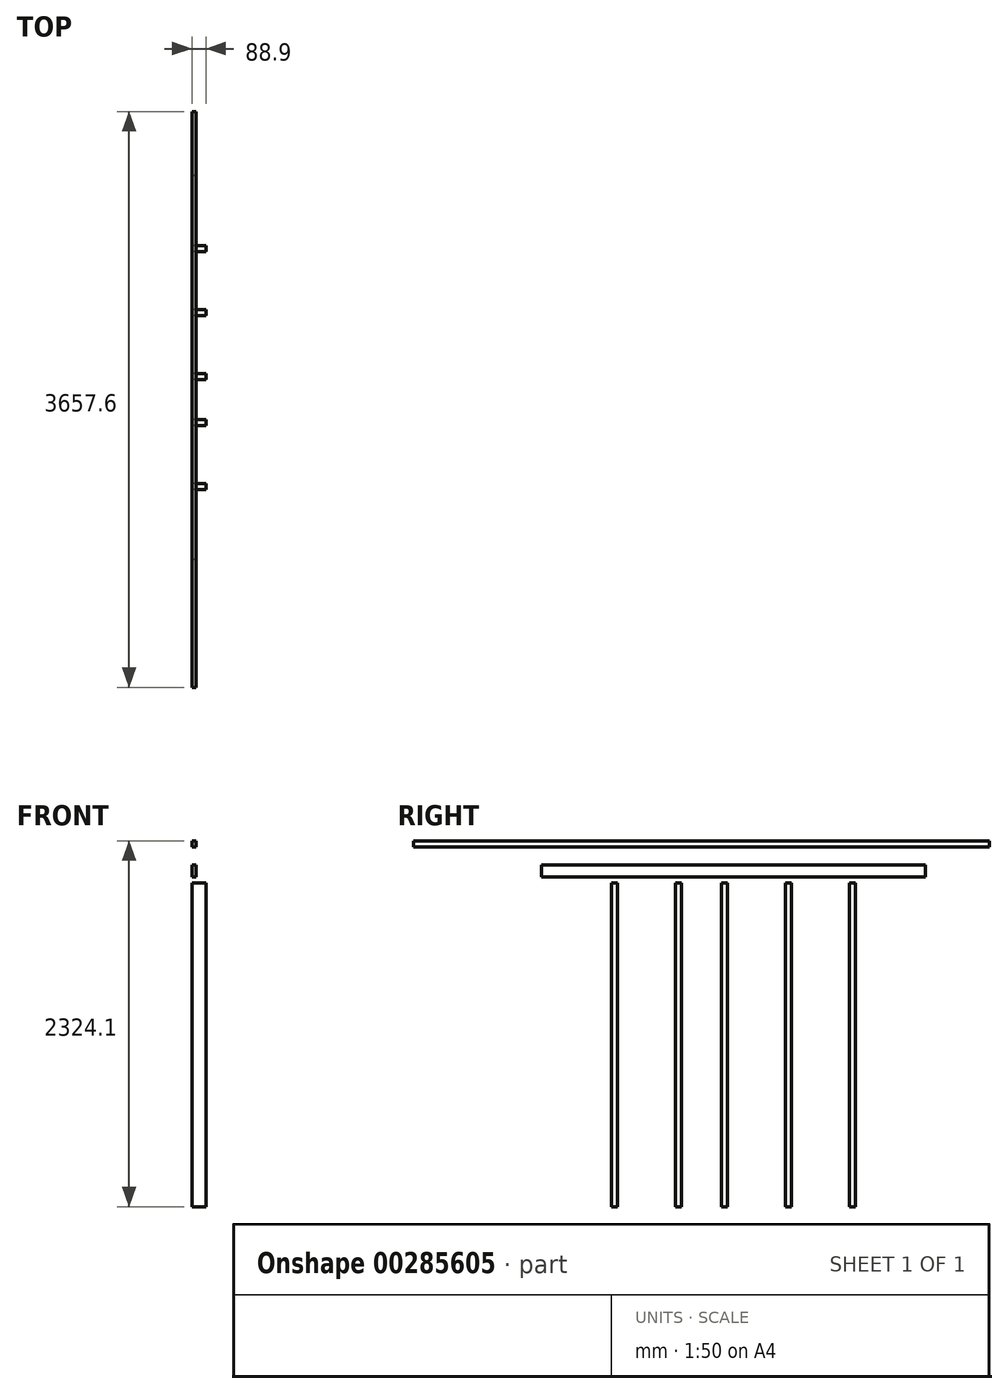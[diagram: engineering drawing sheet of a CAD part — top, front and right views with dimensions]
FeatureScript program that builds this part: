
annotation { "Feature Type Name" : "Feature", "Feature Type Description" : "" }
export const myFeature = defineFeature(function(context is Context, id is Id, definition is map)
    precondition{}
    {
        {
            var Q0;
            Q0=qCreatedBy(makeId("Right.planeOp"),FACE);
            var sketch = newSketch(context, id + "F0", { "sketchPlane" : qUnion([Q0])});
            skLineSegment(sketch, "E0.bottom", {"start": v(-1828.8, -1219.2) * mm, "end": v(1828.8, -1219.2) * mm});
            skLineSegment(sketch, "E0.top", {"start": v(-1828.8, 1219.2) * mm, "end": v(1828.8, 1219.2) * mm});
            skLineSegment(sketch, "E0.left", {"start": v(-1828.8, -1219.2) * mm, "end": v(-1828.8, 1219.2) * mm});
            skLineSegment(sketch, "E0.right", {"start": v(1828.8, -1219.2) * mm, "end": v(1828.8, 1219.2) * mm});
            skPoint(sketch, "E0.middle", {"position": v(0, 0) * mm});
            skLineSegment(sketch, "E1.bottom", {"start": v(-1828.8, -1219.2) * mm, "end": v(0, -1219.2) * mm});
            skLineSegment(sketch, "E1.top", {"start": v(-1828.8, -1181.1) * mm, "end": v(0, -1181.1) * mm});
            skLineSegment(sketch, "E1.left", {"start": v(-1828.8, -1219.2) * mm, "end": v(-1828.8, -1181.1) * mm});
            skLineSegment(sketch, "E2.top", {"start": v(-1828.8, 1181.1) * mm, "end": v(1828.8, 1181.1) * mm});
            skLineSegment(sketch, "E2.left", {"start": v(-1828.8, 1219.2) * mm, "end": v(-1828.8, 1181.1) * mm});
            skLineSegment(sketch, "E2.right", {"start": v(1828.8, 1219.2) * mm, "end": v(1828.8, 1181.1) * mm});
            skLineSegment(sketch, "E3.bottom", {"start": v(-1828.8, 1181.1) * mm, "end": v(0, 1181.1) * mm});
            skLineSegment(sketch, "E3.top", {"start": v(-1828.8, 1143) * mm, "end": v(0, 1143) * mm});
            skLineSegment(sketch, "E3.left", {"start": v(-1828.8, 1181.1) * mm, "end": v(-1828.8, 1143) * mm});
            skLineSegment(sketch, "E4.bottom", {"start": v(0, 1143) * mm, "end": v(1828.8, 1143) * mm});
            skLineSegment(sketch, "E4.top", {"start": v(0, 1181.1) * mm, "end": v(1828.8, 1181.1) * mm});
            skLineSegment(sketch, "E4.right", {"start": v(1828.8, 1143) * mm, "end": v(1828.8, 1181.1) * mm});
            skLineSegment(sketch, "E5.bottom", {"start": v(0, -1219.2) * mm, "end": v(1828.8, -1219.2) * mm});
            skLineSegment(sketch, "E5.top", {"start": v(0, -1181.1) * mm, "end": v(1828.8, -1181.1) * mm});
            skLineSegment(sketch, "E5.right", {"start": v(1828.8, -1219.2) * mm, "end": v(1828.8, -1181.1) * mm});
            skLineSegment(sketch, "E6.bottom", {"start": v(-1828.8, -1181.1) * mm, "end": v(1828.8, -1181.1) * mm});
            skLineSegment(sketch, "E6.top", {"start": v(-1828.8, -1143) * mm, "end": v(1828.8, -1143) * mm});
            skLineSegment(sketch, "E6.left", {"start": v(-1828.8, -1181.1) * mm, "end": v(-1828.8, -1143) * mm});
            skLineSegment(sketch, "E6.right", {"start": v(1828.8, -1181.1) * mm, "end": v(1828.8, -1143) * mm});
            skLineSegment(sketch, "E7.bottom", {"start": v(0, 1143) * mm, "end": v(38.1, 1143) * mm});
            skLineSegment(sketch, "E7.top", {"start": v(0, -1143) * mm, "end": v(38.1, -1143) * mm});
            skLineSegment(sketch, "E8.bottom", {"start": v(0, 1143) * mm, "end": v(-38.1, 1143) * mm});
            skLineSegment(sketch, "E8.top", {"start": v(0, -1143) * mm, "end": v(-38.1, -1143) * mm});
            skLineSegment(sketch, "E9.bottom", {"start": v(1828.8, 1143) * mm, "end": v(1792.72, 1143) * mm});
            skLineSegment(sketch, "E9.top", {"start": v(1828.8, -1143) * mm, "end": v(1792.72, -1143) * mm});
            skLineSegment(sketch, "E9.left", {"start": v(1828.8, 1143) * mm, "end": v(1828.8, -1143) * mm});
            skLineSegment(sketch, "E9.right", {"start": v(1792.72, 1143) * mm, "end": v(1792.72, -1143) * mm});
            skLineSegment(sketch, "E10.bottom", {"start": v(-1828.8, -1143) * mm, "end": v(-1790.7, -1143) * mm});
            skLineSegment(sketch, "E10.top", {"start": v(-1828.8, 1143) * mm, "end": v(-1790.7, 1143) * mm});
            skLineSegment(sketch, "E10.left", {"start": v(-1828.8, -1143) * mm, "end": v(-1828.8, 1143) * mm});
            skLineSegment(sketch, "E10.right", {"start": v(-1790.7, -1143) * mm, "end": v(-1790.7, 1143) * mm});
            skPoint(sketch, "E11.orphan", {"position": v(0, 1219.2) * mm});
            skLineSegment(sketch, "E12", {"start": v(-1828.8, -1143) * mm, "end": v(-1384.3, -1143) * mm});
            skLineSegment(sketch, "E13", {"start": v(-1384.3, -1143) * mm, "end": v(-977.9, -1143) * mm});
            skLineSegment(sketch, "E14", {"start": v(-977.9, -1143) * mm, "end": v(-571.5, -1143) * mm});
            skLineSegment(sketch, "E15", {"start": v(-571.5, -1143) * mm, "end": v(-165.1, -1143) * mm});
            skLineSegment(sketch, "E16.bottom", {"start": v(-1384.3, -1143) * mm, "end": v(-1384.3, -1143) * mm});
            skLineSegment(sketch, "E16.top", {"start": v(-1384.3, 1143) * mm, "end": v(-1384.3, 1143) * mm});
            skLineSegment(sketch, "E16.left", {"start": v(-1384.3, -1143) * mm, "end": v(-1384.3, 1143) * mm});
            skLineSegment(sketch, "E16.right", {"start": v(-1384.3, -1143) * mm, "end": v(-1384.3, 1143) * mm});
            skLineSegment(sketch, "E17.bottom", {"start": v(-977.9, -1143) * mm, "end": v(-977.9, -1143) * mm});
            skLineSegment(sketch, "E17.top", {"start": v(-977.9, 1143) * mm, "end": v(-977.9, 1143) * mm});
            skLineSegment(sketch, "E17.left", {"start": v(-977.9, -1143) * mm, "end": v(-977.9, 990.6) * mm});
            skLineSegment(sketch, "E17.right", {"start": v(-977.9, -1143) * mm, "end": v(-977.9, 990.6) * mm});
            skLineSegment(sketch, "E18.bottom", {"start": v(-571.5, -1143) * mm, "end": v(-571.5, -1143) * mm});
            skLineSegment(sketch, "E18.top", {"start": v(-571.5, 1143) * mm, "end": v(-571.5, 1143) * mm});
            skLineSegment(sketch, "E18.right", {"start": v(-571.5, -1104.9) * mm, "end": v(-571.5, 952.5) * mm});
            skLineSegment(sketch, "E19.bottom", {"start": v(-165.1, -1143) * mm, "end": v(-165.1, -1143) * mm});
            skLineSegment(sketch, "E19.top", {"start": v(-165.1, 1143) * mm, "end": v(-165.1, 1143) * mm});
            skLineSegment(sketch, "E19.left", {"start": v(-165.1, -1104.9) * mm, "end": v(-165.1, 952.5) * mm});
            skLineSegment(sketch, "E19.right", {"start": v(-165.1, -1104.9) * mm, "end": v(-165.1, 952.5) * mm});
            skLineSegment(sketch, "E20", {"start": v(1828.8, -1143) * mm, "end": v(1384.3, -1143) * mm});
            skLineSegment(sketch, "E21", {"start": v(1384.3, -1143) * mm, "end": v(977.9, -1143) * mm});
            skLineSegment(sketch, "E22", {"start": v(977.9, -1143) * mm, "end": v(571.5, -1143) * mm});
            skLineSegment(sketch, "E23", {"start": v(571.5, -1143) * mm, "end": v(165.1, -1143) * mm});
            skLineSegment(sketch, "E24.bottom", {"start": v(1384.3, -1143) * mm, "end": v(1384.3, -1143) * mm});
            skLineSegment(sketch, "E24.top", {"start": v(1384.3, 1143) * mm, "end": v(1384.3, 1143) * mm});
            skLineSegment(sketch, "E24.left", {"start": v(1384.3, -1143) * mm, "end": v(1384.3, 990.6) * mm});
            skLineSegment(sketch, "E24.right", {"start": v(1384.3, -1143) * mm, "end": v(1384.3, 990.6) * mm});
            skLineSegment(sketch, "E25.bottom", {"start": v(977.9, -1143) * mm, "end": v(977.9, -1143) * mm});
            skLineSegment(sketch, "E25.top", {"start": v(977.9, 1143) * mm, "end": v(977.9, 1143) * mm});
            skLineSegment(sketch, "E25.left", {"start": v(977.9, -1104.9) * mm, "end": v(977.9, 952.5) * mm});
            skLineSegment(sketch, "E26.bottom", {"start": v(571.5, -1143) * mm, "end": v(571.5, -1143) * mm});
            skLineSegment(sketch, "E26.top", {"start": v(571.5, 1143) * mm, "end": v(571.5, 1143) * mm});
            skLineSegment(sketch, "E26.left", {"start": v(571.5, -1104.9) * mm, "end": v(571.5, 952.5) * mm});
            skLineSegment(sketch, "E26.right", {"start": v(571.5, -1104.9) * mm, "end": v(571.5, 952.5) * mm});
            skLineSegment(sketch, "E27.bottom", {"start": v(165.1, -1143) * mm, "end": v(165.1, -1143) * mm});
            skLineSegment(sketch, "E27.top", {"start": v(165.1, 1143) * mm, "end": v(165.1, 1143) * mm});
            skLineSegment(sketch, "E27.left", {"start": v(165.1, -1104.9) * mm, "end": v(165.1, 952.5) * mm});
            skLineSegment(sketch, "E27.right", {"start": v(165.1, -1104.9) * mm, "end": v(165.1, 952.5) * mm});
            skLineSegment(sketch, "E28.bottom", {"start": v(1384.3, -1143) * mm, "end": v(1346.2, -1143) * mm});
            skLineSegment(sketch, "E28.top", {"start": v(1384.3, 1143) * mm, "end": v(1346.2, 1143) * mm});
            skLineSegment(sketch, "E28.right", {"start": v(1346.2, -1143) * mm, "end": v(1346.2, 990.6) * mm});
            skLineSegment(sketch, "E29.bottom", {"start": v(977.9, -1143) * mm, "end": v(939.8, -1143) * mm});
            skLineSegment(sketch, "E29.top", {"start": v(977.9, 1143) * mm, "end": v(939.8, 1143) * mm});
            skLineSegment(sketch, "E29.right", {"start": v(939.8, -1104.9) * mm, "end": v(939.8, 952.5) * mm});
            skLineSegment(sketch, "E30.bottom", {"start": v(571.5, -1143) * mm, "end": v(533.4, -1143) * mm});
            skLineSegment(sketch, "E30.top", {"start": v(571.5, 1143) * mm, "end": v(533.4, 1143) * mm});
            skLineSegment(sketch, "E30.right", {"start": v(533.4, -1104.9) * mm, "end": v(533.4, 952.5) * mm});
            skLineSegment(sketch, "E31.bottom", {"start": v(-1384.3, -1143) * mm, "end": v(-1346.2, -1143) * mm});
            skLineSegment(sketch, "E31.top", {"start": v(-1384.3, 1143) * mm, "end": v(-1346.2, 1143) * mm});
            skLineSegment(sketch, "E31.right", {"start": v(-1346.2, -1143) * mm, "end": v(-1346.2, 1143) * mm});
            skLineSegment(sketch, "E32.bottom", {"start": v(-977.9, -1143) * mm, "end": v(-939.8, -1143) * mm});
            skLineSegment(sketch, "E32.top", {"start": v(-977.9, 1143) * mm, "end": v(-939.8, 1143) * mm});
            skLineSegment(sketch, "E32.right", {"start": v(-939.8, -1143) * mm, "end": v(-939.8, 990.6) * mm});
            skLineSegment(sketch, "E33.bottom", {"start": v(-571.5, -1143) * mm, "end": v(-533.4, -1143) * mm});
            skLineSegment(sketch, "E33.top", {"start": v(-571.5, 1143) * mm, "end": v(-533.4, 1143) * mm});
            skLineSegment(sketch, "E33.right", {"start": v(-533.4, -1104.9) * mm, "end": v(-533.4, 952.5) * mm});
            skLineSegment(sketch, "E34.bottom", {"start": v(-165.1, -1143) * mm, "end": v(-127, -1143) * mm});
            skLineSegment(sketch, "E34.top", {"start": v(-165.1, 1143) * mm, "end": v(-127, 1143) * mm});
            skLineSegment(sketch, "E34.right", {"start": v(-127, -1104.9) * mm, "end": v(-127, 952.5) * mm});
            skLineSegment(sketch, "E35.bottom", {"start": v(165.1, -1143) * mm, "end": v(127, -1143) * mm});
            skLineSegment(sketch, "E35.top", {"start": v(165.1, 1143) * mm, "end": v(127, 1143) * mm});
            skLineSegment(sketch, "E35.right", {"start": v(127, -1104.9) * mm, "end": v(127, 952.5) * mm});
            skLineSegment(sketch, "E36.bottom", {"start": v(1792.72, -1143) * mm, "end": v(1754.62, -1143) * mm});
            skLineSegment(sketch, "E36.top", {"start": v(1792.72, 1143) * mm, "end": v(1754.62, 1143) * mm});
            skLineSegment(sketch, "E36.left", {"start": v(1792.72, -1143) * mm, "end": v(1792.72, 1143) * mm});
            skLineSegment(sketch, "E36.right", {"start": v(1754.62, -1143) * mm, "end": v(1754.62, 1143) * mm});
            skLineSegment(sketch, "E37.bottom", {"start": v(-1790.7, -1143) * mm, "end": v(-1752.6, -1143) * mm});
            skLineSegment(sketch, "E37.top", {"start": v(-1790.7, 1143) * mm, "end": v(-1752.6, 1143) * mm});
            skLineSegment(sketch, "E37.right", {"start": v(-1752.6, -1143) * mm, "end": v(-1752.6, 1143) * mm});
            skLineSegment(sketch, "E38", {"start": v(0, -1143) * mm, "end": v(0, 990.6) * mm});
            skLineSegment(sketch, "E39", {"start": v(0, 990.6) * mm, "end": v(1346.2, 990.6) * mm});
            skLineSegment(sketch, "E40", {"start": v(1346.2, 990.6) * mm, "end": v(1346.2, -1143) * mm});
            skLineSegment(sketch, "E41", {"start": v(0, 990.6) * mm, "end": v(-939.8, 990.6) * mm});
            skLineSegment(sketch, "E42", {"start": v(-939.8, 990.6) * mm, "end": v(-939.8, -1143) * mm});
            skLineSegment(sketch, "E43.top", {"start": v(0, 952.5) * mm, "end": v(1346.2, 952.5) * mm});
            skLineSegment(sketch, "E43.left", {"start": v(0, 990.6) * mm, "end": v(0, 952.5) * mm});
            skLineSegment(sketch, "E43.right", {"start": v(1346.2, 990.6) * mm, "end": v(1346.2, 952.5) * mm});
            skLineSegment(sketch, "E44.top", {"start": v(0, 952.5) * mm, "end": v(-939.8, 952.5) * mm});
            skLineSegment(sketch, "E44.right", {"start": v(-939.8, 990.6) * mm, "end": v(-939.8, 952.5) * mm});
            skLineSegment(sketch, "E45.bottom", {"start": v(-939.8, -1143) * mm, "end": v(0, -1143) * mm});
            skLineSegment(sketch, "E45.top", {"start": v(-939.8, -1104.9) * mm, "end": v(0, -1104.9) * mm});
            skLineSegment(sketch, "E45.left", {"start": v(-939.8, -1143) * mm, "end": v(-939.8, -1104.9) * mm});
            skLineSegment(sketch, "E45.right", {"start": v(0, -1143) * mm, "end": v(0, -1104.9) * mm});
            skLineSegment(sketch, "E46.bottom", {"start": v(0, -1143) * mm, "end": v(1346.2, -1143) * mm});
            skLineSegment(sketch, "E46.top", {"start": v(0, -1104.9) * mm, "end": v(1346.2, -1104.9) * mm});
            skLineSegment(sketch, "E46.right", {"start": v(1346.2, -1143) * mm, "end": v(1346.2, -1104.9) * mm});
            skLineSegment(sketch, "E47.bottom", {"start": v(0, 952.5) * mm, "end": v(-38.1, 952.5) * mm});
            skLineSegment(sketch, "E47.top", {"start": v(0, -1104.9) * mm, "end": v(-38.1, -1104.9) * mm});
            skLineSegment(sketch, "E47.left", {"start": v(0, 952.5) * mm, "end": v(0, -1104.9) * mm});
            skLineSegment(sketch, "E47.right", {"start": v(-38.1, 952.5) * mm, "end": v(-38.1, -1104.9) * mm});
            skLineSegment(sketch, "E48.bottom", {"start": v(0, 952.5) * mm, "end": v(38.1, 952.5) * mm});
            skLineSegment(sketch, "E48.top", {"start": v(0, -1104.9) * mm, "end": v(38.1, -1104.9) * mm});
            skLineSegment(sketch, "E48.right", {"start": v(38.1, 952.5) * mm, "end": v(38.1, -1104.9) * mm});
            skLineSegment(sketch, "E49.bottom", {"start": v(-939.8, 952.5) * mm, "end": v(-901.7, 952.5) * mm});
            skLineSegment(sketch, "E49.top", {"start": v(-939.8, -1104.9) * mm, "end": v(-901.7, -1104.9) * mm});
            skLineSegment(sketch, "E49.left", {"start": v(-939.8, 952.5) * mm, "end": v(-939.8, -1104.9) * mm});
            skLineSegment(sketch, "E49.right", {"start": v(-901.7, 952.5) * mm, "end": v(-901.7, -1104.9) * mm});
            skLineSegment(sketch, "E50.bottom", {"start": v(1346.2, 952.5) * mm, "end": v(1308.1, 952.5) * mm});
            skLineSegment(sketch, "E50.top", {"start": v(1346.2, -1104.9) * mm, "end": v(1308.1, -1104.9) * mm});
            skLineSegment(sketch, "E50.left", {"start": v(1346.2, 952.5) * mm, "end": v(1346.2, -1104.9) * mm});
            skLineSegment(sketch, "E50.right", {"start": v(1308.1, 952.5) * mm, "end": v(1308.1, -1104.9) * mm});
            skLineSegment(sketch, "E51.bottom", {"start": v(1346.2, 990.6) * mm, "end": v(-939.8, 990.6) * mm});
            skLineSegment(sketch, "E51.top", {"start": v(1346.2, 1066.8) * mm, "end": v(-939.8, 1066.8) * mm});
            skLineSegment(sketch, "E52.top", {"start": v(1346.2, 1028.7) * mm, "end": v(-939.8, 1028.7) * mm});
            skLineSegment(sketch, "E53", {"start": v(977.9, 1066.8) * mm, "end": v(977.9, 1143) * mm});
            skLineSegment(sketch, "E54", {"start": v(939.8, 1066.8) * mm, "end": v(939.8, 1143) * mm});
            skLineSegment(sketch, "E55", {"start": v(571.5, 1066.8) * mm, "end": v(571.5, 1143) * mm});
            skLineSegment(sketch, "E56", {"start": v(533.4, 1066.8) * mm, "end": v(533.4, 1143) * mm});
            skLineSegment(sketch, "E57", {"start": v(165.1, 1066.8) * mm, "end": v(165.1, 1143) * mm});
            skLineSegment(sketch, "E58", {"start": v(127, 1066.8) * mm, "end": v(127, 1143) * mm});
            skLineSegment(sketch, "E59", {"start": v(-127, 1066.8) * mm, "end": v(-127, 1143) * mm});
            skLineSegment(sketch, "E60", {"start": v(-165.1, 1066.8) * mm, "end": v(-165.1, 1143) * mm});
            skLineSegment(sketch, "E61", {"start": v(-533.4, 1066.8) * mm, "end": v(-533.4, 1143) * mm});
            skPoint(sketch, "E62.trimOffspring.start.orphan", {"position": v(977.9, 990.6) * mm});
            skLineSegment(sketch, "E63.trimOffspring", {"start": v(-571.5, 1066.8) * mm, "end": v(-571.5, 1143) * mm});
            skLineSegment(sketch, "E64.bottom", {"start": v(-977.9, 1143) * mm, "end": v(-1016, 1143) * mm});
            skLineSegment(sketch, "E64.top", {"start": v(-977.9, -1143) * mm, "end": v(-1016, -1143) * mm});
            skLineSegment(sketch, "E64.left", {"start": v(-977.9, 1143) * mm, "end": v(-977.9, 1066.8) * mm});
            skLineSegment(sketch, "E64.right", {"start": v(-1016, 1143) * mm, "end": v(-1016, -1143) * mm});
            skLineSegment(sketch, "E65.bottom", {"start": v(1384.3, 1143) * mm, "end": v(1422.4, 1143) * mm});
            skLineSegment(sketch, "E65.top", {"start": v(1384.3, -1143) * mm, "end": v(1422.4, -1143) * mm});
            skLineSegment(sketch, "E65.left", {"start": v(1384.3, 1143) * mm, "end": v(1384.3, 1066.8) * mm});
            skLineSegment(sketch, "E65.right", {"start": v(1422.4, 1143) * mm, "end": v(1422.4, -1143) * mm});
            skLineSegment(sketch, "E66", {"start": v(-939.8, 1066.8) * mm, "end": v(-1016, 1066.8) * mm});
            skLineSegment(sketch, "E67", {"start": v(-939.8, 1028.7) * mm, "end": v(-1016, 1028.7) * mm});
            skLineSegment(sketch, "E68", {"start": v(-939.8, 990.6) * mm, "end": v(-1016, 990.6) * mm});
            skLineSegment(sketch, "E69", {"start": v(1346.2, 1066.8) * mm, "end": v(1422.4, 1066.8) * mm});
            skLineSegment(sketch, "E70", {"start": v(1346.2, 1028.7) * mm, "end": v(1422.4, 1028.7) * mm});
            skLineSegment(sketch, "E71", {"start": v(1346.2, 990.6) * mm, "end": v(1422.4, 990.6) * mm});
            skLineSegment(sketch, "E72.trimOffspring", {"start": v(1346.2, 1066.8) * mm, "end": v(1346.2, 1143) * mm});
            skLineSegment(sketch, "E73.trimOffspring", {"start": v(1384.3, 1066.8) * mm, "end": v(1384.3, 1143) * mm});
            skLineSegment(sketch, "E74.trimOffspring", {"start": v(1384.3, 990.6) * mm, "end": v(1384.3, -1143) * mm});
            skLineSegment(sketch, "E75.trimOffspring", {"start": v(-939.8, 1066.8) * mm, "end": v(-939.8, 1143) * mm});
            skLineSegment(sketch, "E76.trimOffspring", {"start": v(-977.9, 990.6) * mm, "end": v(-977.9, -1143) * mm});
            skLineSegment(sketch, "E77.trimOffspring", {"start": v(-977.9, 1066.8) * mm, "end": v(-977.9, 1143) * mm});
            skSolve(sketch);
        }
        {
            var Q0;
            {var subQ0=sQuery(id+"F0.wireOp",EDGE,"E43.right");Q0=makeQuery(id+"F0.imprint","IMPRINT",FACE,{"disambiguationData":[TD([[makeQuery(id+"F0.imprint","IMPRINT",EDGE,{"derivedFrom":subQ0}),-1.0]])]});}
            var Q1;
            Q1=makeQuery(id+"F0.imprint","IMPRINT",FACE,{"disambiguationData":[TD([[makeQuery(id+"F0.imprint","IMPRINT",EDGE,{"derivedFrom":sQuery(id+"F0.wireOp",EDGE,"E48.bottom")}),-1.0]])]});
            var Q2;
            {var subQ0=sQuery(id+"F0.wireOp",EDGE,"E27.left");Q2=makeQuery(id+"F0.imprint","IMPRINT",FACE,{"disambiguationData":[TD([[makeQuery(id+"F0.imprint","IMPRINT",EDGE,{"derivedFrom":subQ0}),1.0]])]});}
            var Q3;
            {var subQ11=sQuery(id+"F0.wireOp",EDGE,"E45.right");Q3=makeQuery(id+"F0.imprint","IMPRINT",FACE,{"disambiguationData":[TD([[makeQuery(id+"F0.imprint","IMPRINT",EDGE,{"derivedFrom":subQ11}),-1.0]])]});}
            var Q4;
            {var subQ0=sQuery(id+"F0.wireOp",EDGE,"E26.left");Q4=makeQuery(id+"F0.imprint","IMPRINT",FACE,{"disambiguationData":[TD([[makeQuery(id+"F0.imprint","IMPRINT",EDGE,{"derivedFrom":subQ0}),1.0]])]});}
            var Q5;
            {var subQ0=sQuery(id+"F0.wireOp",EDGE,"E25.left");Q5=makeQuery(id+"F0.imprint","IMPRINT",FACE,{"disambiguationData":[TD([[makeQuery(id+"F0.imprint","IMPRINT",EDGE,{"derivedFrom":subQ0}),1.0]])]});}
            var Q6;
            Q6=makeQuery(id+"F0.imprint","IMPRINT",FACE,{"disambiguationData":[TD([[makeQuery(id+"F0.imprint","IMPRINT",EDGE,{"derivedFrom":sQuery(id+"F0.wireOp",EDGE,"E50.bottom")}),1.0]])]});
            extrude(context, id + "F1", {"entities" : qUnion([Q0, Q1, Q2, Q3, Q4, Q5, Q6]), "depth" : 88.9 * mm});
        }
        {
            var Q0;
            {var subQ7=sQuery(id+"F0.wireOp",EDGE,"E43.left");Q0=makeQuery(id+"F0.imprint","IMPRINT",FACE,{"disambiguationData":[TD([[makeQuery(id+"F0.imprint","IMPRINT",EDGE,{"derivedFrom":subQ7}),-1.0]])]});}
            var Q1;
            Q1=makeQuery(id+"F0.imprint","IMPRINT",FACE,{"disambiguationData":[TD([[makeQuery(id+"F0.imprint","IMPRINT",EDGE,{"derivedFrom":sQuery(id+"F0.wireOp",EDGE,"E47.bottom")}),1.0]])]});
            var Q2;
            {var subQ0=sQuery(id+"F0.wireOp",EDGE,"E19.left");Q2=makeQuery(id+"F0.imprint","IMPRINT",FACE,{"disambiguationData":[TD([[makeQuery(id+"F0.imprint","IMPRINT",EDGE,{"derivedFrom":subQ0}),-1.0]])]});}
            var Q3;
            {var subQ0=sQuery(id+"F0.wireOp",EDGE,"E18.right");Q3=makeQuery(id+"F0.imprint","IMPRINT",FACE,{"disambiguationData":[TD([[makeQuery(id+"F0.imprint","IMPRINT",EDGE,{"derivedFrom":subQ0}),-1.0]])]});}
            var Q4;
            Q4=makeQuery(id+"F0.imprint","IMPRINT",FACE,{"disambiguationData":[TD([[makeQuery(id+"F0.imprint","IMPRINT",EDGE,{"derivedFrom":sQuery(id+"F0.wireOp",EDGE,"E49.bottom")}),-1.0]])]});
            var Q5;
            {var subQ10=sQuery(id+"F0.wireOp",EDGE,"E45.left");Q5=makeQuery(id+"F0.imprint","IMPRINT",FACE,{"disambiguationData":[TD([[makeQuery(id+"F0.imprint","IMPRINT",EDGE,{"derivedFrom":subQ10}),-1.0]])]});}
            extrude(context, id + "F2", {"entities" : qUnion([Q0, Q1, Q2, Q3, Q4, Q5]), "depth" : 88.9 * mm});
        }
        {
            var Q0;
            Q0=makeQuery(id+"F0.imprint","IMPRINT",FACE,{"disambiguationData":[TD([[makeQuery(id+"F0.imprint","IMPRINT",EDGE,{"derivedFrom":sQuery(id+"F0.wireOp",EDGE,"E0.top")}),-1.0]])]});
            var Q1;
            Q1=makeQuery(id+"F0.imprint","IMPRINT",FACE,{"disambiguationData":[TD([[makeQuery(id+"F0.imprint","IMPRINT",EDGE,{"derivedFrom":sQuery(id+"F0.wireOp",EDGE,"E3.bottom")}),-1.0]])]});
            var Q2;
            Q2=makeQuery(id+"F0.imprint","IMPRINT",FACE,{"disambiguationData":[TD([[makeQuery(id+"F0.imprint","IMPRINT",EDGE,{"derivedFrom":sQuery(id+"F0.wireOp",EDGE,"E52.top")}),-1.0]])]});
            var Q3;
            Q3=makeQuery(id+"F0.imprint","IMPRINT",FACE,{"disambiguationData":[TD([[makeQuery(id+"F0.imprint","IMPRINT",EDGE,{"derivedFrom":sQuery(id+"F0.wireOp",EDGE,"E52.top")}),1.0]])]});
            var Q4;
            Q4=makeQuery(id+"F0.imprint","IMPRINT",FACE,{"disambiguationData":[TD([[makeQuery(id+"F0.imprint","IMPRINT",EDGE,{"derivedFrom":sQuery(id+"F0.wireOp",EDGE,"E6.bottom")}),1.0]])]});
            var Q5;
            Q5=makeQuery(id+"F0.imprint","IMPRINT",FACE,{"disambiguationData":[TD([[makeQuery(id+"F0.imprint","IMPRINT",EDGE,{"derivedFrom":sQuery(id+"F0.wireOp",EDGE,"E1.bottom")}),1.0]])]});
            var Q6;
            Q6=makeQuery(id+"F0.imprint","IMPRINT",FACE,{"disambiguationData":[TD([[makeQuery(id+"F0.imprint","IMPRINT",EDGE,{"derivedFrom":sQuery(id+"F0.wireOp",EDGE,"E9.bottom")}),1.0]])]});
            var Q7;
            Q7=makeQuery(id+"F0.imprint","IMPRINT",FACE,{"disambiguationData":[TD([[makeQuery(id+"F0.imprint","IMPRINT",EDGE,{"derivedFrom":sQuery(id+"F0.wireOp",EDGE,"E36.bottom")}),-1.0]])]});
            var Q8;
            {var subQ0=sQuery(id+"F0.wireOp",EDGE,"E65.top");Q8=makeQuery(id+"F0.imprint","IMPRINT",FACE,{"disambiguationData":[TD([[makeQuery(id+"F0.imprint","IMPRINT",EDGE,{"derivedFrom":subQ0}),1.0]])]});}
            var Q9;
            Q9=makeQuery(id+"F0.imprint","IMPRINT",FACE,{"disambiguationData":[TD([[makeQuery(id+"F0.imprint","IMPRINT",EDGE,{"derivedFrom":sQuery(id+"F0.wireOp",EDGE,"E28.bottom")}),-1.0]])]});
            var Q10;
            Q10=makeQuery(id+"F0.imprint","IMPRINT",FACE,{"disambiguationData":[TD([[makeQuery(id+"F0.imprint","IMPRINT",EDGE,{"derivedFrom":sQuery(id+"F0.wireOp",EDGE,"E32.bottom")}),1.0]])]});
            var Q11;
            {var subQ0=sQuery(id+"F0.wireOp",EDGE,"E64.top");Q11=makeQuery(id+"F0.imprint","IMPRINT",FACE,{"disambiguationData":[TD([[makeQuery(id+"F0.imprint","IMPRINT",EDGE,{"derivedFrom":subQ0}),-1.0]])]});}
            var Q12;
            Q12=makeQuery(id+"F0.imprint","IMPRINT",FACE,{"disambiguationData":[TD([[makeQuery(id+"F0.imprint","IMPRINT",EDGE,{"derivedFrom":sQuery(id+"F0.wireOp",EDGE,"E31.bottom")}),1.0]])]});
            var Q13;
            Q13=makeQuery(id+"F0.imprint","IMPRINT",FACE,{"disambiguationData":[TD([[makeQuery(id+"F0.imprint","IMPRINT",EDGE,{"derivedFrom":sQuery(id+"F0.wireOp",EDGE,"E37.bottom")}),1.0]])]});
            var Q14;
            Q14=makeQuery(id+"F0.imprint","IMPRINT",FACE,{"disambiguationData":[TD([[makeQuery(id+"F0.imprint","IMPRINT",EDGE,{"derivedFrom":sQuery(id+"F0.wireOp",EDGE,"E10.top")}),-1.0]])]});
            var Q15;
            {var subQ0=sQuery(id+"F0.wireOp",EDGE,"E64.bottom");Q15=makeQuery(id+"F0.imprint","IMPRINT",FACE,{"disambiguationData":[TD([[makeQuery(id+"F0.imprint","IMPRINT",EDGE,{"derivedFrom":subQ0}),1.0]])]});}
            var Q16;
            Q16=makeQuery(id+"F0.imprint","IMPRINT",FACE,{"disambiguationData":[TD([[makeQuery(id+"F0.imprint","IMPRINT",EDGE,{"derivedFrom":sQuery(id+"F0.wireOp",EDGE,"E32.top")}),-1.0]])]});
            var Q17;
            Q17=makeQuery(id+"F0.imprint","IMPRINT",FACE,{"disambiguationData":[TD([[makeQuery(id+"F0.imprint","IMPRINT",EDGE,{"derivedFrom":sQuery(id+"F0.wireOp",EDGE,"E33.top")}),-1.0]])]});
            var Q18;
            Q18=makeQuery(id+"F0.imprint","IMPRINT",FACE,{"disambiguationData":[TD([[makeQuery(id+"F0.imprint","IMPRINT",EDGE,{"derivedFrom":sQuery(id+"F0.wireOp",EDGE,"E34.top")}),-1.0]])]});
            var Q19;
            Q19=makeQuery(id+"F0.imprint","IMPRINT",FACE,{"disambiguationData":[TD([[makeQuery(id+"F0.imprint","IMPRINT",EDGE,{"derivedFrom":sQuery(id+"F0.wireOp",EDGE,"E35.top")}),1.0]])]});
            var Q20;
            Q20=makeQuery(id+"F0.imprint","IMPRINT",FACE,{"disambiguationData":[TD([[makeQuery(id+"F0.imprint","IMPRINT",EDGE,{"derivedFrom":sQuery(id+"F0.wireOp",EDGE,"E30.top")}),1.0]])]});
            var Q21;
            Q21=makeQuery(id+"F0.imprint","IMPRINT",FACE,{"disambiguationData":[TD([[makeQuery(id+"F0.imprint","IMPRINT",EDGE,{"derivedFrom":sQuery(id+"F0.wireOp",EDGE,"E29.top")}),1.0]])]});
            var Q22;
            Q22=makeQuery(id+"F0.imprint","IMPRINT",FACE,{"disambiguationData":[TD([[makeQuery(id+"F0.imprint","IMPRINT",EDGE,{"derivedFrom":sQuery(id+"F0.wireOp",EDGE,"E28.top")}),1.0]])]});
            var Q23;
            {var subQ0=sQuery(id+"F0.wireOp",EDGE,"E65.bottom");Q23=makeQuery(id+"F0.imprint","IMPRINT",FACE,{"disambiguationData":[TD([[makeQuery(id+"F0.imprint","IMPRINT",EDGE,{"derivedFrom":subQ0}),-1.0]])]});}
            extrude(context, id + "F3", {"entities" : qUnion([Q0, Q1, Q2, Q3, Q4, Q5, Q6, Q7, Q8, Q9, Q10, Q11, Q12, Q13, Q14, Q15, Q16, Q17, Q18, Q19, Q20, Q21, Q22, Q23]), "depth" : 25.4 * mm});
        }
    });
